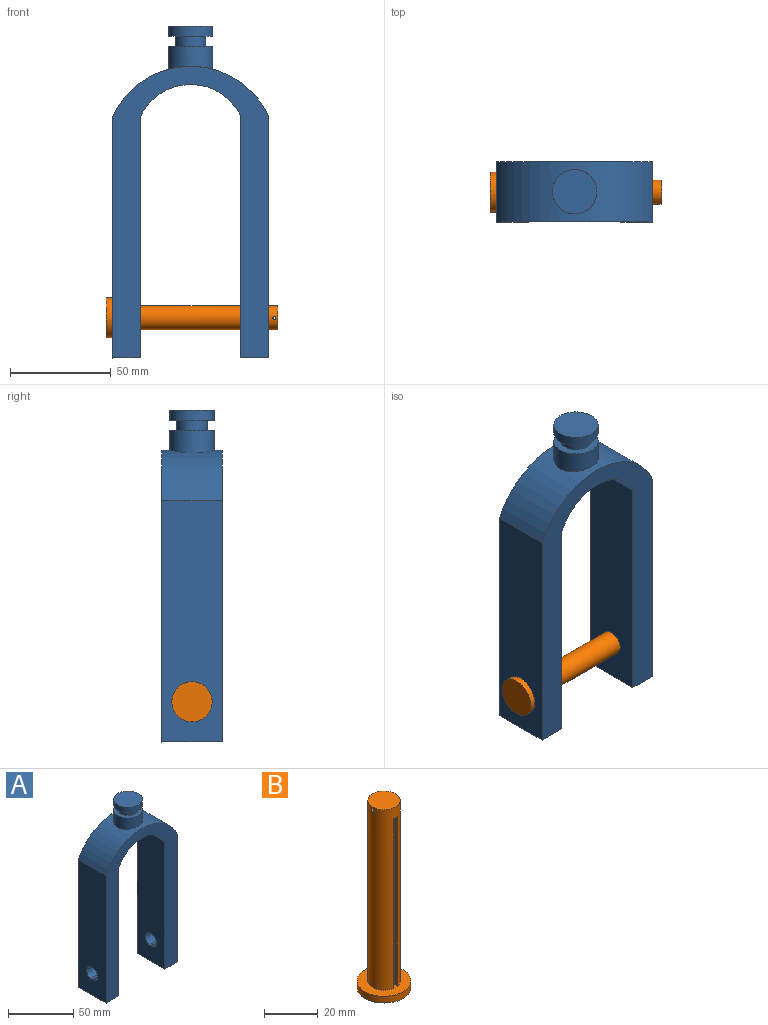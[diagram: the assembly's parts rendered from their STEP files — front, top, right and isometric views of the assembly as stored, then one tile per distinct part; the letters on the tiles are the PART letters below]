
ASSEMBLY  parts=2 mates=1
PART A: 24 faces, bbox 77.7x30x165 mm
  f0: cylinder r=11mm len=22mm, axis (0,0,-1), area 743.1mm2, adj f1,f21
  f1: cylinder r=42.7mm len=77.69mm, axis (0,1,0), area 2543.4mm2, adj f0,f4,f10,f11,f12
  f2: cylinder r=6mm len=13.84mm, axis (1,0,0), area 495.4mm2, adj f4,f6,f16,f18
  f3: cylinder r=6mm len=13.84mm, axis (1,0,0), area 495.4mm2, adj f8,f10,f13,f15
  f4: plane 120x30mm, normal (-1,0,0), area 3489.5mm2, adj f1,f2,f5,f11,f12,f16,f17,f18
  f5: plane 30x13.84mm, normal (0,0,-1), area 415.3mm2, adj f4,f6,f11,f12
  f6: plane 120x30mm, normal (1,0,0), area 3489.5mm2, adj f2,f5,f7,f11,f12,f16,f17,f18
  f7: cylinder r=27.6mm len=50mm, axis (0,1,0), area 1876.8mm2, adj f6,f8,f11,f12
  f8: plane 120x30mm, normal (-1,0,0), area 3489.5mm2, adj f3,f7,f9,f11,f12,f13,f14,f15
  f9: plane 30x13.84mm, normal (0,0,-1), area 415.3mm2, adj f8,f10,f11,f12
  f10: plane 120x30mm, normal (1,0,0), area 3489.5mm2, adj f1,f3,f9,f11,f12,f13,f14,f15
  f11: plane 144.97x77.69mm, normal (0,-1,0), area 4145.5mm2, adj f1,f4,f5,f6,f7,f8,f9,f10
  f12: plane 144.97x77.69mm, normal (0,1,0), area 4145.5mm2, adj f1,f4,f5,f6,f7,f8,f9,f10
  f13: plane 13.84x1.3mm, normal (0,-1,0), area 18mm2, adj f3,f8,f10,f14
  f14: plane 13.84x1.9mm, normal (0,0,1), area 26.3mm2, adj f8,f10,f13,f15
  f15: plane 13.84x1.3mm, normal (0,1,0), area 18mm2, adj f3,f8,f10,f14
  f16: plane 13.84x1.3mm, normal (0,-1,0), area 18mm2, adj f2,f4,f6,f17
  f17: plane 13.84x1.9mm, normal (0,0,1), area 26.3mm2, adj f4,f6,f16,f18
  f18: plane 13.84x1.3mm, normal (0,1,0), area 18mm2, adj f2,f4,f6,f17
  f19: cylinder r=7.5mm len=15mm, axis (0,0,-1), area 235.6mm2, adj f20,f21
  f20: plane 22x22mm, normal (0,0,-1), area 203.4mm2, adj f19,f23
  f21: plane 22x22mm, normal (0,0,1), area 203.4mm2, adj f0,f19
  f22: plane 22x22mm, normal (0,0,1), area 380.1mm2, adj f23
  f23: cylinder r=11mm len=22mm, axis (0,0,-1), area 345.6mm2, adj f20,f22
PART B: 10 faces, bbox 20x20x85 mm
  f0: cylinder r=6mm len=82mm, axis (0,0,-1), area 2925.2mm2, adj f1,f3,f5,f6,f7,f8
  f1: plane 12x12mm, normal (0,0,1), area 113.1mm2, adj f0
  f2: cylinder r=10mm len=20mm, axis (0,0,-1), area 188.5mm2, adj f3,f4
  f3: plane 20x20mm, normal (0,0,1), area 204.5mm2, adj f0,f2,f7,f8,f9
  f4: plane 20x20mm, normal (0,0,-1), area 314.2mm2, adj f2
  f5: cylinder r=0.75mm len=12mm, axis (-1,0,0), area 56.3mm2, adj f0
  f6: plane 2.1x1.68mm, normal (0,0,-1), area 3.5mm2, adj f0,f7,f8,f9
  f7: plane 77x1.6mm, normal (1,0,0), area 123mm2, adj f0,f3,f6,f9
  f8: plane 77x1.58mm, normal (-1,0,0), area 121.8mm2, adj f0,f3,f6,f9
  f9: plane 77x2.1mm, normal (0,-1,0), area 161.7mm2, adj f3,f6,f7,f8
PLACE A t=(-61.79,26.3,36.38)mm
PLACE B rot(axis=(0.58,0.58,0.58),120deg) t=(-103.63,11.3,56.38)mm
MATE slider B.f0 <-> A.f2  axis (1,0,0) through (-100.63,11.3,56.38)mm
